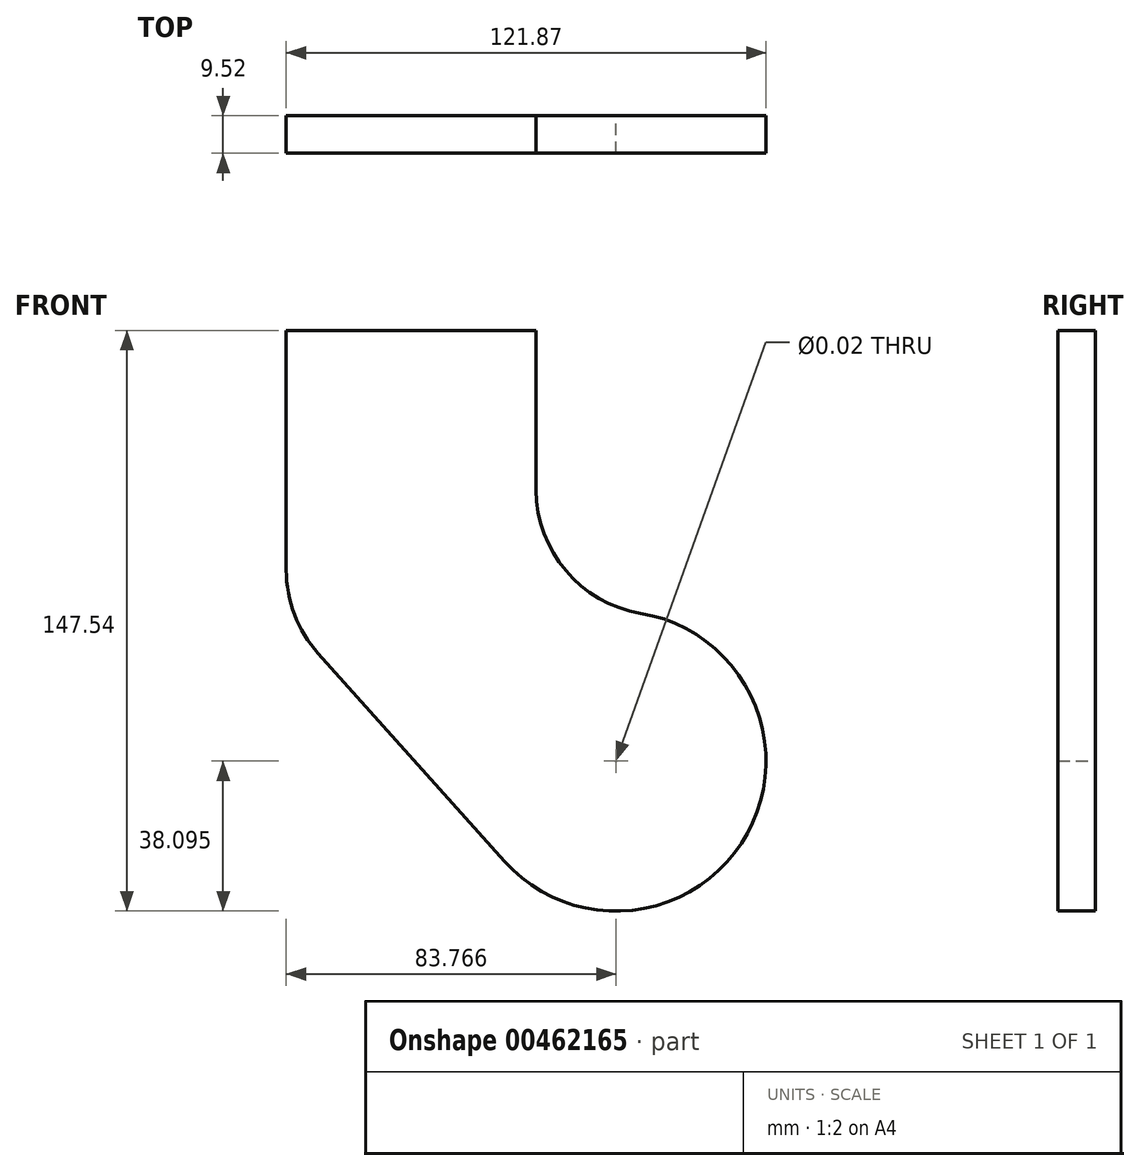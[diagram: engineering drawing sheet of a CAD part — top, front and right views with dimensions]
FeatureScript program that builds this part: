
annotation { "Feature Type Name" : "Feature", "Feature Type Description" : "" }
export const myFeature = defineFeature(function(context is Context, id is Id, definition is map)
    precondition{}
    {
        {
            var Q0;
            Q0=qCreatedBy(makeId("Front.planeOp"),FACE);
            var sketch = newSketch(context, id + "F0", { "sketchPlane" : qUnion([Q0])});
            skLineSegment(sketch, "E0.top", {"start": v(31.75, 36.51) * mm, "end": v(-31.75, 36.51) * mm});
            skLineSegment(sketch, "E0.left", {"start": v(31.75, -36.51) * mm, "end": v(31.75, 36.51) * mm});
            skLineSegment(sketch, "E0.right", {"start": v(-31.75, -36.51) * mm, "end": v(-31.75, 36.51) * mm});
            skPoint(sketch, "E0.middle", {"position": v(0, 0) * mm});
            skLineSegment(sketch, "E1", {"start": v(0, -36.51) * mm, "end": v(52.02, -72.93) * mm, "construction": true});
            skLineSegment(sketch, "E2", {"start": v(0, 36.51) * mm, "end": v(0, -36.51) * mm, "construction": true});
            skArc(sketch, "E3", {"start": v(35.81, -92.5) * mm, "mid": v(73.67, -86.2) * mm, "end": v(62.09, -49.62) * mm});
            skLineSegment(sketch, "E4", {"start": v(31.75, -36.51) * mm, "end": v(62.09, -49.62) * mm});
            skLineSegment(sketch, "E5", {"start": v(-31.75, -36.51) * mm, "end": v(35.81, -92.5) * mm});
            skCircle(sketch, "E6", {"center": v(52.02, -72.93) * mm, "radius": 38.1 * mm});
            skLineSegment(sketch, "E7", {"start": v(31.75, -36.51) * mm, "end": v(48.58, -34.99) * mm});
            skLineSegment(sketch, "E8", {"start": v(-31.75, -36.51) * mm, "end": v(23.63, -98.35) * mm});
            skSolve(sketch);
        }
        {
            var Q0;
            Q0=makeQuery(id+"F0.imprint","IMPRINT",FACE,{"disambiguationData":[TD([[makeQuery(id+"F0.imprint","IMPRINT",EDGE,{"derivedFrom":sQuery(id+"F0.wireOp",EDGE,"E0.top")}),1.0]])]});
            var Q1;
            {var subQ0=sQuery(id+"F0.wireOp",EDGE,"E3");Q1=makeQuery(id+"F0.imprint","IMPRINT",FACE,{"disambiguationData":[TD([[makeQuery(id+"F0.imprint","IMPRINT",EDGE,{"derivedFrom":subQ0}),1.0]])]});}
            var Q2;
            {var subQ0=sQuery(id+"F0.wireOp",EDGE,"E3");Q2=makeQuery(id+"F0.imprint","IMPRINT",FACE,{"disambiguationData":[TD([[makeQuery(id+"F0.imprint","IMPRINT",EDGE,{"derivedFrom":subQ0}),-1.0]])]});}
            var Q3;
            {var subQ0=sQuery(id+"F0.wireOp",EDGE,"E4");var subQ1=sQuery(id+"F0.wireOp",EDGE,"E0.left");var subQ2=makeQuery(id+"F0.imprint","INTERSECT",VERTEX,{"derivedFrom":[subQ1,subQ0]});Q3=makeQuery(id+"F0.imprint","IMPRINT",FACE,{"disambiguationData":[TD([[makeQuery(id+"F0.imprint","IMPRINT",EDGE,{"disambiguationData":[TD([[subQ2,-1.0]])],"derivedFrom":subQ1}),-1.0]])]});}
            var Q4;
            {var subQ0=sQuery(id+"F0.wireOp",EDGE,"E8");Q4=makeQuery(id+"F0.imprint","IMPRINT",FACE,{"disambiguationData":[TD([[makeQuery(id+"F0.imprint","IMPRINT",EDGE,{"derivedFrom":subQ0}),1.0]])]});}
            var Q5;
            {var subQ0=sQuery(id+"F0.wireOp",EDGE,"E7");Q5=makeQuery(id+"F0.imprint","IMPRINT",FACE,{"disambiguationData":[TD([[makeQuery(id+"F0.imprint","IMPRINT",EDGE,{"derivedFrom":subQ0}),-1.0]])]});}
            extrude(context, id + "F1", {"entities" : qUnion([Q0, Q1, Q2, Q3, Q4, Q5]), "depth" : 9.52 * mm, "symmetric" : true});
        }
        {
            var Q0;
            Q0=makeQuery(id+"F1.opExtrude","CAP_FACE",FACE,{"disambiguationData":[OSD([sQuery(id+"F0.wireOp",EDGE,"E0.top"),sQuery(id+"F0.wireOp",EDGE,"E0.left"),sQuery(id+"F0.wireOp",EDGE,"E0.right"),sQuery(id+"F0.wireOp",EDGE,"E3"),sQuery(id+"F0.wireOp",EDGE,"E4"),sQuery(id+"F0.wireOp",EDGE,"E5")])],"isStart":false});
            var sketch = newSketch(context, id + "F2", { "sketchPlane" : qUnion([Q0])});
            skPoint(sketch, "E9", {"position": v(52.02, -72.93) * mm});
            skSolve(sketch);
        }
        {
            var Q0;
            Q0=sQuery(id+"F2.wireOp",VERTEX,"E9");
            var Q1;
            Q1=makeQuery(id+"F1.opExtrude","SWEPT_BODY",BODY,{"disambiguationData":[OSD([sQuery(id+"F0.wireOp",EDGE,"E0.top"),sQuery(id+"F0.wireOp",EDGE,"E0.left"),sQuery(id+"F0.wireOp",EDGE,"E0.right"),sQuery(id+"F0.wireOp",EDGE,"E3"),sQuery(id+"F0.wireOp",EDGE,"E4"),sQuery(id+"F0.wireOp",EDGE,"E5")])]});
            hole(context, id + "F3", {"style" : HoleStyle.SIMPLE, "endStyle" : HoleEndStyle.THROUGH, "standardTappedOrClearance" : lookupTablePath({ "standard" : "ANSI", "size" : "1/2 (0.5)", "type" : "Drilled" }), "standardBlindInLast" : lookupTablePath({ "standard" : "ANSI", "size" : "1/2", "type" : "Drilled" }), "holeDiameter" : 1 / 50.8 * mm, "isTappedThrough" : true, "tappedDepth" : 57.15 * mm, "tapClearance" : 3, "locations" : qUnion([Q0]), "scope" : qUnion([Q1]), "startStyle" : HoleStartStyle.SKETCH});
        }
        {
            var Q0;
            Q0=makeQuery(id+"F1.opExtrude","SWEPT_EDGE",EDGE,{"disambiguationData":[OSD([sQuery(id+"F0.wireOp",EDGE,"E0.right"),sQuery(id+"F0.wireOp",EDGE,"E5"),sQuery(id+"F0.wireOp",EDGE,"E8")])]});
            var Q1;
            Q1=makeQuery(id+"F1.opExtrude","SWEPT_EDGE",EDGE,{"disambiguationData":[OSD([sQuery(id+"F0.wireOp",EDGE,"E0.left"),sQuery(id+"F0.wireOp",EDGE,"E4"),sQuery(id+"F0.wireOp",EDGE,"E7")])]});
            fillet(context, id + "F4", {"entities" : qUnion([Q0, Q1]), "radius" : 31.75 * mm, "tangentPropagation" : true, "allowEdgeOverflow" : false});
        }
    });
